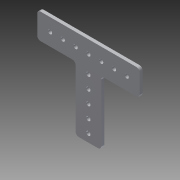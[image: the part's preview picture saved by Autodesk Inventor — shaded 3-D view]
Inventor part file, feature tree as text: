
AUTODESK INVENTOR PART (.ipt)
format: ipt  version: 2014 (Build 180170000, 170)  size: 121,344 bytes
history: native  units: in
note: dims shown in document units (in); Inventor stores cm internally (conversion verified against a paired STEP export)
features: extrude x1, fillet x1, sketch x1
ambient origin geometry x8: Origin, YZ Plane, XZ Plane, XY Plane, X Axis, Y Axis, Z Axis, Center Point
bodies: Solid1 (feature_tree)
feature tree (3):
  extrude  "Extrusion1"  Depth=1.0in
  fillet  "Fillet1"  Radius=1.5in
  sketch  "Sketch1"  dims[d0=4.0in d1=1.0in d2=1.5in d3=1.0in d4=3.5in d5=0.163in d6=0.5in d7=0.5in d8=2.7559in d10=0.5in d11=0.3937in d13=1.0in d15=0.1875in d16=1.9685in d18=0.5in d19=0.3937in d21=1.0in d23=0.5in d24=0.125in d25=0.0in d26=0.125in]
